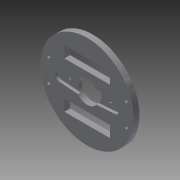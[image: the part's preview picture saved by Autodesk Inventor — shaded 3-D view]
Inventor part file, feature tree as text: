
AUTODESK INVENTOR PART (.ipt)
format: ipt  version: 2015 (Build 190159000, 159)  size: 153,600 bytes
history: native  units: mm
features: extrude x3, sketch x3, fillet x1
ambient origin geometry x8: Origin, YZ Plane, XZ Plane, XY Plane, X Axis, Y Axis, Z Axis, Center Point
bodies: Body1 (feature_tree)
feature tree (7):
  extrude  "Extrusion4"  Depth=10.0mm
  extrude  "Extrusion5"  Depth=20.0mm
  fillet  "Fillet1"  Radius=3.3mm
  extrude  "Extrusion6"  Depth=5.0mm
  sketch  "Sketch3"  dims[d4=74.558575mm d5=60.588575mm d7=10.0mm]
  sketch  "Sketch5"  dims[d8=3.0mm d9=20.0mm d11=20.0mm d12=20.0mm d14=68.0mm d17=3.3mm]
  sketch  "Sketch7"  dims[d18=18.0mm d19=2.0mm d21=5.0mm d22=10.0mm d27=5.0mm d28=0.0mm d30=13.0mm d31=28.0mm d32=4.5mm d33=4.5mm d34=2.5mm d35=0.0mm d36=4.0mm d39=20.0mm d40=5.0mm d41=0.0mm]
